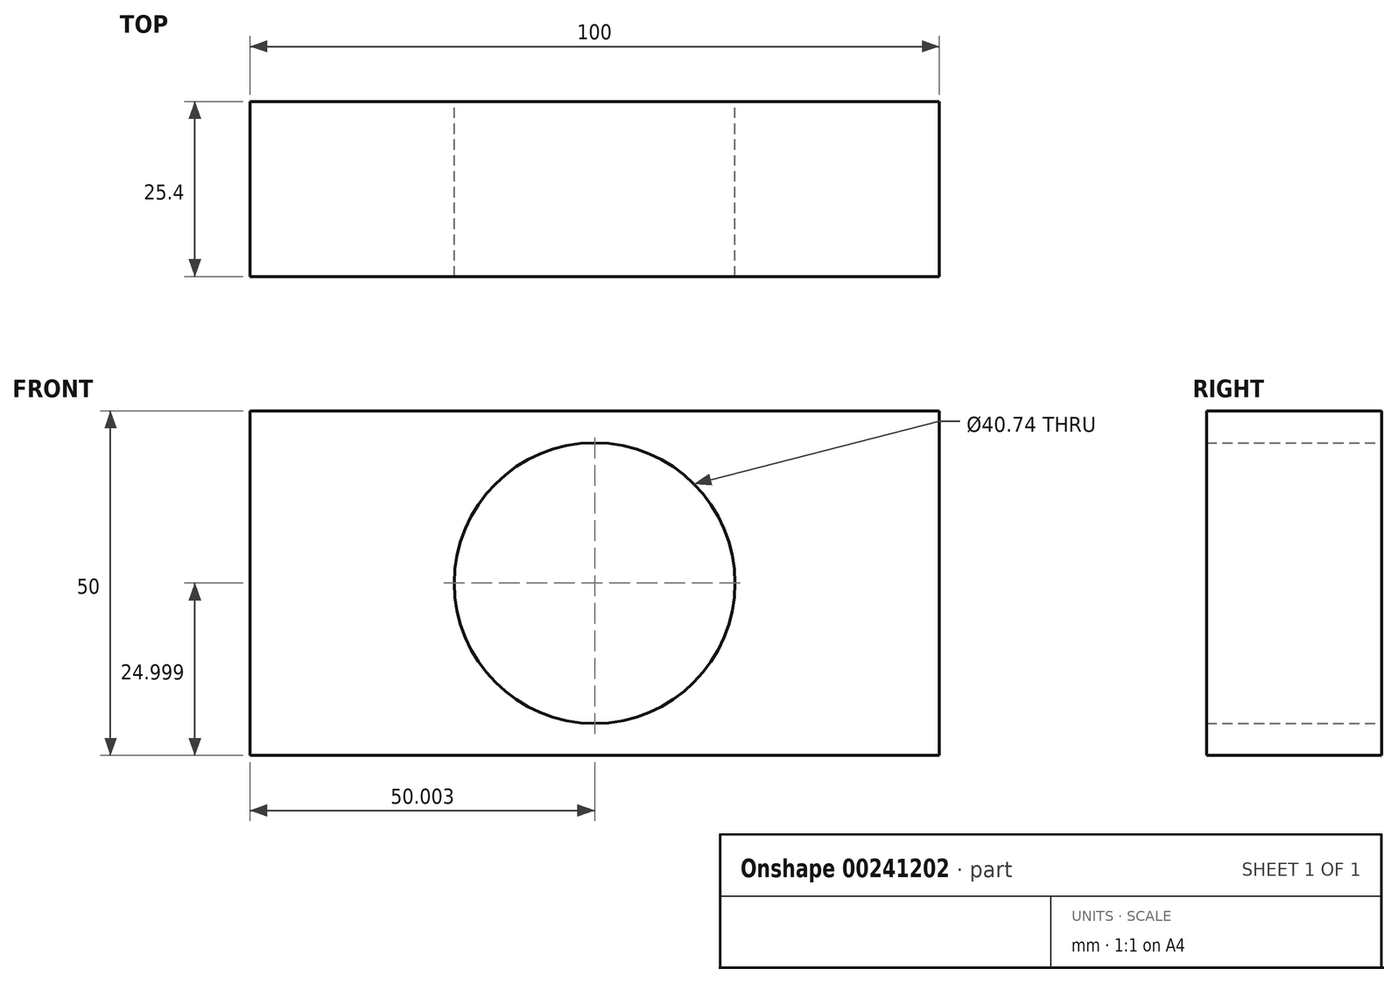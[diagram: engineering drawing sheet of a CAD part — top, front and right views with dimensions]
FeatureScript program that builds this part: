
annotation { "Feature Type Name" : "Feature", "Feature Type Description" : "" }
export const myFeature = defineFeature(function(context is Context, id is Id, definition is map)
    precondition{}
    {
        {
            var Q0;
            Q0=qCreatedBy(makeId("Front.planeOp"),FACE);
            var sketch = newSketch(context, id + "F0", { "sketchPlane" : qUnion([Q0])});
            skLineSegment(sketch, "E0", {"start": v(-56.5, 70.28) * mm, "end": v(43.5, 70.28) * mm});
            skLineSegment(sketch, "E1", {"start": v(-56.5, 70.28) * mm, "end": v(-56.5, 20.28) * mm});
            skLineSegment(sketch, "E2", {"start": v(-56.5, 20.28) * mm, "end": v(43.5, 20.28) * mm});
            skLineSegment(sketch, "E3", {"start": v(43.5, 20.28) * mm, "end": v(43.5, 70.28) * mm});
            skCircle(sketch, "E4", {"center": v(-6.5, 45.28) * mm, "radius": 20.37 * mm});
            skSolve(sketch);
        }
        {
            var Q0;
            Q0=makeQuery(id+"F0.imprint","IMPRINT",FACE,{"disambiguationData":[TD([[makeQuery(id+"F0.imprint","IMPRINT",EDGE,{"derivedFrom":sQuery(id+"F0.wireOp",EDGE,"E0")}),-1.0]])]});
            extrude(context, id + "F1", {"entities" : qUnion([Q0]), "depth" : 25.4 * mm});
        }
    });
